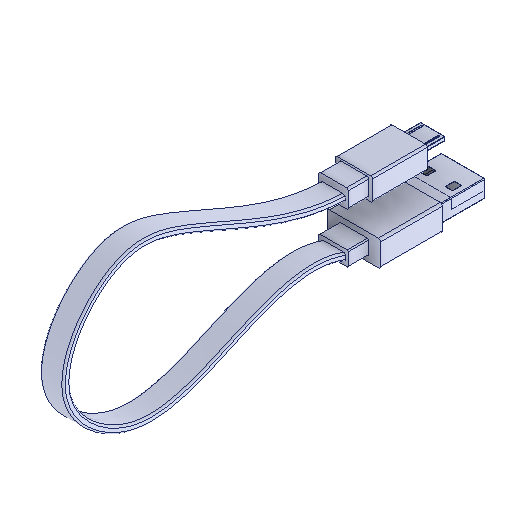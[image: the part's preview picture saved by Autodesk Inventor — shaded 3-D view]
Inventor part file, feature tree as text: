
AUTODESK INVENTOR PART (.ipt)
format: ipt  version: 2024.1 (Build 281209000, 209)  size: 298,496 bytes
history: native  units: mm
features: other x4, sweep x1
ambient origin geometry x8: Origin, YZ Plane, XZ Plane, XY Plane, X Axis, Y Axis, Z Axis, Center Point
bodies: Volumenkörper1 (feature_tree), Volumenkörper2 (feature_tree), Volumenkörper3 (feature_tree), Volumenkörper4 (feature_tree), Volumenkörper5 (feature_tree)
feature tree (5):
  other  "Cut-Extrude1"
  other  "Cut-Extrude2"
  other  "Cut-Extrude3"
  other  "Boss-Extrude8"
  sweep  "Sweep1"
